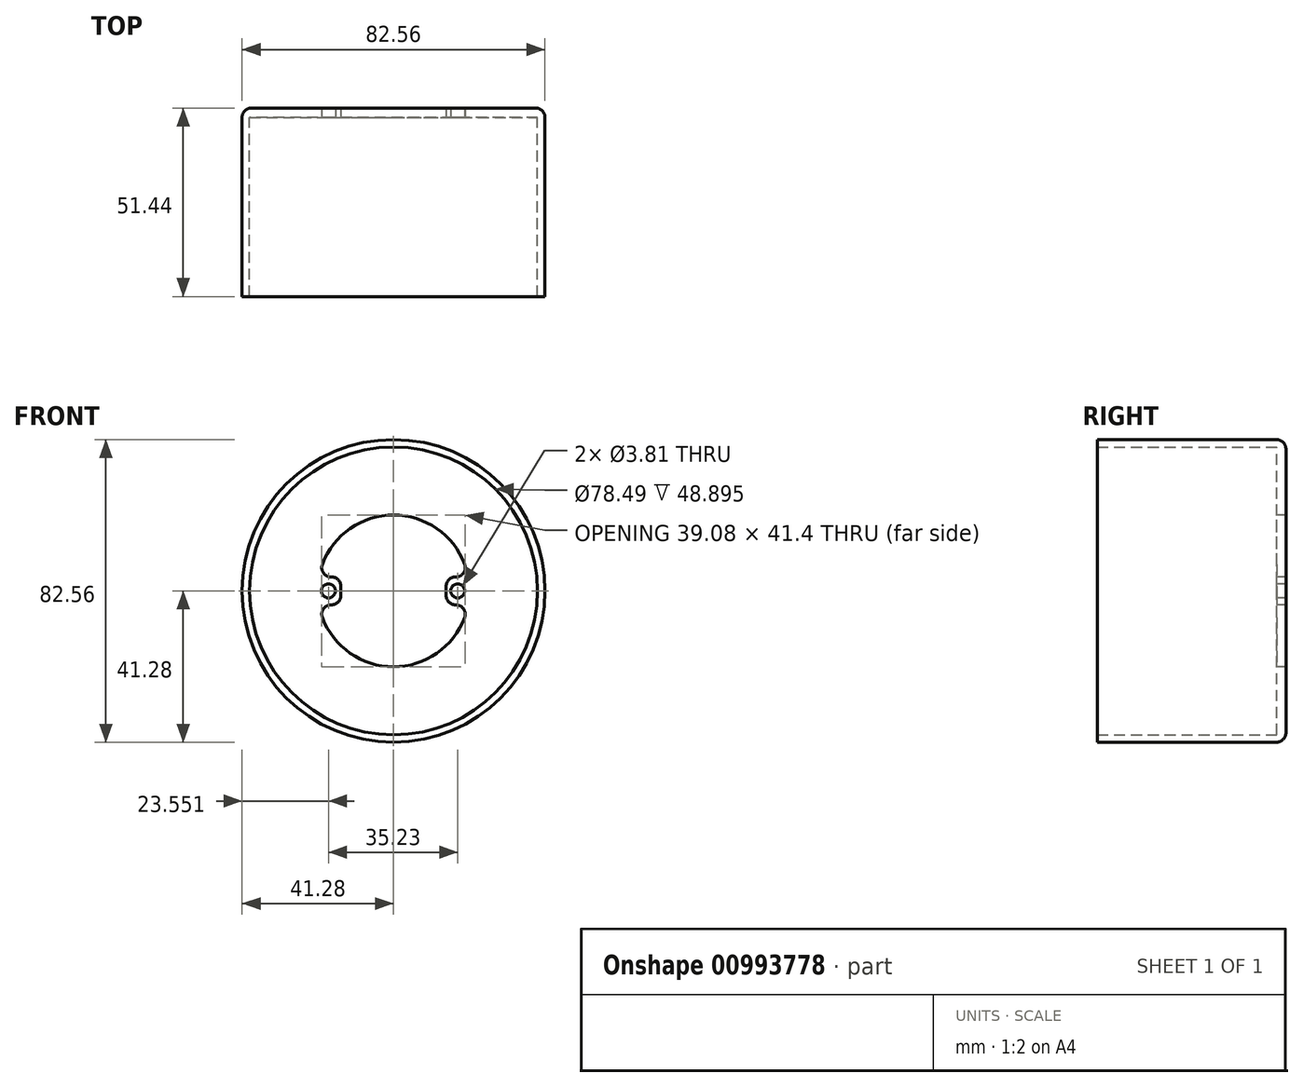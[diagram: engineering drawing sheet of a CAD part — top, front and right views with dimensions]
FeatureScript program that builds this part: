
annotation { "Feature Type Name" : "Feature", "Feature Type Description" : "" }
export const myFeature = defineFeature(function(context is Context, id is Id, definition is map)
    precondition{}
    {
        {
            var Q0;
            Q0=qCreatedBy(makeId("Front.planeOp"),FACE);
            var sketch = newSketch(context, id + "F0", { "sketchPlane" : qUnion([Q0])});
            skCircle(sketch, "E0", {"center": v(0, 0) * mm, "radius": 41.28 * mm});
            skSolve(sketch);
        }
        {
            var Q0;
            Q0=makeQuery(id+"F0.imprint","IMPRINT",FACE,{"disambiguationData":[TD([[makeQuery(id+"F0.imprint","IMPRINT",EDGE,{"derivedFrom":sQuery(id+"F0.wireOp",EDGE,"E0")}),1.0]])]});
            extrude(context, id + "F1", {"entities" : qUnion([Q0]), "depth" : 2.54 * mm, "offsetDistance" : 25.4 * mm});
        }
        {
            var Q0;
            Q0=makeQuery(id+"F1.opExtrude","CAP_FACE",FACE,{"disambiguationData":[OSD([sQuery(id+"F0.wireOp",EDGE,"E0")])],"isStart":false});
            var sketch = newSketch(context, id + "F2", { "sketchPlane" : qUnion([Q0])});
            skCircle(sketch, "E1", {"center": v(0, 0) * mm, "radius": 20.7 * mm});
            skCircle(sketch, "E2", {"center": v(17.5, 0) * mm, "radius": 1.9 * mm});
            skCircle(sketch, "E3", {"center": v(-17.73, 0) * mm, "radius": 1.9 * mm});
            skLineSegment(sketch, "E4.bottom", {"start": v(20.7, 3.81) * mm, "end": v(14.35, 3.8) * mm});
            skLineSegment(sketch, "E4.top", {"start": v(20.7, -3.81) * mm, "end": v(14.35, -3.81) * mm});
            skLineSegment(sketch, "E4.left", {"start": v(20.7, 3.81) * mm, "end": v(20.7, -3.81) * mm});
            skLineSegment(sketch, "E4.right", {"start": v(14.35, 3.81) * mm, "end": v(14.35, -3.81) * mm});
            skLineSegment(sketch, "E5.MirrorCS", {"start": v(-14.35, 3.81) * mm, "end": v(-14.35, -3.81) * mm});
            skLineSegment(sketch, "E6.MirrorCS", {"start": v(-20.7, 3.81) * mm, "end": v(-14.35, 3.8) * mm});
            skLineSegment(sketch, "E7.MirrorCS", {"start": v(-20.7, 3.81) * mm, "end": v(-20.7, -3.81) * mm});
            skLineSegment(sketch, "E8.MirrorCS", {"start": v(-20.7, -3.81) * mm, "end": v(-14.35, -3.81) * mm});
            skSolve(sketch);
        }
        {
            var Q0;
            Q0=makeQuery(id+"F1.opExtrude","CAP_FACE",FACE,{"disambiguationData":[OSD([sQuery(id+"F0.wireOp",EDGE,"E0")])],"isStart":false});
            var sketch = newSketch(context, id + "F3", { "sketchPlane" : qUnion([Q0])});
            skCircle(sketch, "E9", {"center": v(0, 0) * mm, "radius": 41.27 * mm});
            skCircle(sketch, "E10", {"center": v(0, 0) * mm, "radius": 39.24 * mm});
            skSolve(sketch);
        }
        {
            var Q0;
            Q0=makeQuery(id+"F3.imprint","IMPRINT",FACE,{"disambiguationData":[TD([[makeQuery(id+"F3.imprint","IMPRINT",EDGE,{"derivedFrom":sQuery(id+"F3.wireOp",EDGE,"E9")}),1.0]])]});
            extrude(context, id + "F4", {"entities" : qUnion([Q0]), "operationType" : NewBodyOperationType.ADD, "depth" : 48.9 * mm, "offsetDistance" : 25.4 * mm});
        }
        {
            var Q0;
            Q0=makeQuery(id+"F1.opExtrude","CAP_EDGE",EDGE,{"disambiguationData":[OSD([sQuery(id+"F0.wireOp",EDGE,"E0")])],"isStart":true});
            fillet(context, id + "F5", {"entities" : qUnion([Q0]), "radius" : 2.54 * mm, "tangentPropagation" : true, "allowEdgeOverflow" : false});
        }
        {
            var Q0;
            Q0=makeQuery(id+"F2.imprint","IMPRINT",FACE,{"disambiguationData":[TD([[makeQuery(id+"F2.imprint","IMPRINT",EDGE,{"derivedFrom":sQuery(id+"F2.wireOp",EDGE,"E2")}),1.0]])]});
            var Q1;
            Q1=makeQuery(id+"F2.imprint","IMPRINT",FACE,{"disambiguationData":[TD([[makeQuery(id+"F2.imprint","IMPRINT",EDGE,{"derivedFrom":sQuery(id+"F2.wireOp",EDGE,"E3")}),1.0]])]});
            var Q2;
            {var subQ0=sQuery(id+"F2.wireOp",EDGE,"E4.right");Q2=makeQuery(id+"F2.imprint","IMPRINT",FACE,{"disambiguationData":[TD([[makeQuery(id+"F2.imprint","IMPRINT",EDGE,{"derivedFrom":subQ0}),-1.0]])]});}
            extrude(context, id + "F6", {"entities" : qUnion([Q0, Q1, Q2]), "operationType" : NewBodyOperationType.REMOVE, "oppositeDirection" : true, "depth" : 25.4 * mm, "offsetDistance" : 25.4 * mm, "hasSecondDirection" : true, "secondDirectionOppositeDirection" : false, "secondDirectionDepth" : 25.4 * mm});
        }
        {
            var Q0;
            Q0=makeQuery(id+"F6.boolean.opBoolean","COPY",EDGE,{"derivedFrom":makeQuery(id+"F6.opExtrude","SWEPT_EDGE",EDGE,{"disambiguationData":[OSD([sQuery(id+"F2.wireOp",EDGE,"E1"),sQuery(id+"F2.wireOp",EDGE,"E6.MirrorCS")])]})});
            var Q1;
            Q1=makeQuery(id+"F6.boolean.opBoolean","COPY",EDGE,{"derivedFrom":makeQuery(id+"F6.opExtrude","SWEPT_EDGE",EDGE,{"disambiguationData":[OSD([sQuery(id+"F2.wireOp",EDGE,"E5.MirrorCS"),sQuery(id+"F2.wireOp",EDGE,"E6.MirrorCS")])]})});
            var Q2;
            Q2=makeQuery(id+"F6.boolean.opBoolean","COPY",EDGE,{"derivedFrom":makeQuery(id+"F6.opExtrude","SWEPT_EDGE",EDGE,{"disambiguationData":[OSD([sQuery(id+"F2.wireOp",EDGE,"E5.MirrorCS"),sQuery(id+"F2.wireOp",EDGE,"E8.MirrorCS")])]})});
            var Q3;
            Q3=makeQuery(id+"F6.boolean.opBoolean","COPY",EDGE,{"derivedFrom":makeQuery(id+"F6.opExtrude","SWEPT_EDGE",EDGE,{"disambiguationData":[OSD([sQuery(id+"F2.wireOp",EDGE,"E1"),sQuery(id+"F2.wireOp",EDGE,"E8.MirrorCS")])]})});
            var Q4;
            Q4=makeQuery(id+"F6.boolean.opBoolean","COPY",EDGE,{"derivedFrom":makeQuery(id+"F6.opExtrude","SWEPT_EDGE",EDGE,{"disambiguationData":[OSD([sQuery(id+"F2.wireOp",EDGE,"E4.bottom"),sQuery(id+"F2.wireOp",EDGE,"E4.right")])]})});
            var Q5;
            Q5=makeQuery(id+"F6.boolean.opBoolean","COPY",EDGE,{"derivedFrom":makeQuery(id+"F6.opExtrude","SWEPT_EDGE",EDGE,{"disambiguationData":[OSD([sQuery(id+"F2.wireOp",EDGE,"E4.top"),sQuery(id+"F2.wireOp",EDGE,"E4.right")])]})});
            var Q6;
            Q6=makeQuery(id+"F6.boolean.opBoolean","COPY",EDGE,{"derivedFrom":makeQuery(id+"F6.opExtrude","SWEPT_EDGE",EDGE,{"disambiguationData":[OSD([sQuery(id+"F2.wireOp",EDGE,"E1"),sQuery(id+"F2.wireOp",EDGE,"E4.top")])]})});
            var Q7;
            Q7=makeQuery(id+"F6.boolean.opBoolean","COPY",EDGE,{"derivedFrom":makeQuery(id+"F6.opExtrude","SWEPT_EDGE",EDGE,{"disambiguationData":[OSD([sQuery(id+"F2.wireOp",EDGE,"E1"),sQuery(id+"F2.wireOp",EDGE,"E4.bottom")])]})});
            fillet(context, id + "F7", {"entities" : qUnion([Q0, Q1, Q2, Q3, Q4, Q5, Q6, Q7]), "tangentPropagation" : true, "radius" : 2.54 * mm, "defaultsChanged" : false, "vertexSettings" : [], "allowEdgeOverflow" : false});
        }
    });
